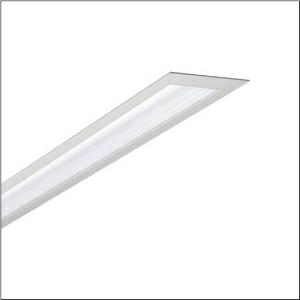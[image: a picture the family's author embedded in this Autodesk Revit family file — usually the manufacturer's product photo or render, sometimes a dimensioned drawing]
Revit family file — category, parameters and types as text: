
# Revit family: silica_r_5mx12wd1w4a_d237
name_source: partatom
category: Lighting Fixtures
units: mm (PartAtom-declared; Revit-internal decimal feet)

## family parameters
Cut with Voids When Loaded = No
Host = Face
Light Source = No
Part Type = Normal
Room Calculation Point = No
Round Connector Dimension = Use Diameter
Shared = No

## types (1)
- --- (1 x LED, 4680 lm, 29.3 W, 4000K)
    Apparent Load = 29 VA
    CIE Flux Codes = 70 95 99 100 100
    Color Rendering = 80
    Color Temperature = 4000K
    Default Elevation = 1800 mm
    Description = Silica®, office luminaire, primary light control with wallwasher, of aluminium, light emission: direct distribution, primary light characteristic: asymmetric, installation type: recessed, LED rated luminous flux: 4.680 lm, light colour: 840, colour temperature: 4000K, control gear: ECG DALI, with terminal, 3+2-pole, max. 2.5mm², mains connection: 230V, AC, 50/60Hz, rated input power: 29W, luminaire housing, of aluminium, matt pure white (RAL 9010), length: 1.462 mm, width: 93 mm, height: 60mm, end cap, of diecast zinc, pure white (RAL 9010), protection rating (complete): IP20, insulation class (complete): insulation class I (protective earthing), certification: CE, permissible ambient temperature for indoor applications: 0..+35°C, standard: EN 50419, packaging unit: 1 piece
    Height = 0 mm  [stored 0 ft]
    Lamp = 1 x LED
    Lamp Light Flux = 4680 lm
    Lamp Power = 29.3 W
    Lamp count = 1
    Length = 1462 mm
    Luminous efficacy = 160 lm/W
    Manufacturer = Siteco
    ModVariant = No
    Model = 5MX12WD1W4A
    Mounting Place = Ceiling
    Mounting Type = Recessed
    Number of Poles = 1
    OnlyDefault = Yes
    Power Factor = 1
    Product Name = Silica®
    Product group = office luminaire | ceiling recessed
    ProductGroupID = 400
    Protection Class = Protection class I
    Protection Degree = IP 20
    RLX_Detail_Level = 1
    RlxData = <blob elided: 24645 chars, md5=e552393b>
    Socket = socket
    Standby Power = 0 W
    System Light Flux = 4680 lm
    System Power = 29 W
    Type Comments = factory setting: luminous flux: 100 % | dim-lin: 254 | 164 mA
    Type Image = l_1004825.jpg
    URL = http://relux.com
    VarID = @adj_131770
    Voltage = 0 V
    Weight = 0.00 kg
    Width = 93 mm

note: [stored X ft] marks values corroborated as IEEE doubles in the binary element streams (Revit-internal decimal feet)

## geometry (parser evidence)
native form markers: Blend x4, Sweep x11
no freeform markers — native parametric forms only
